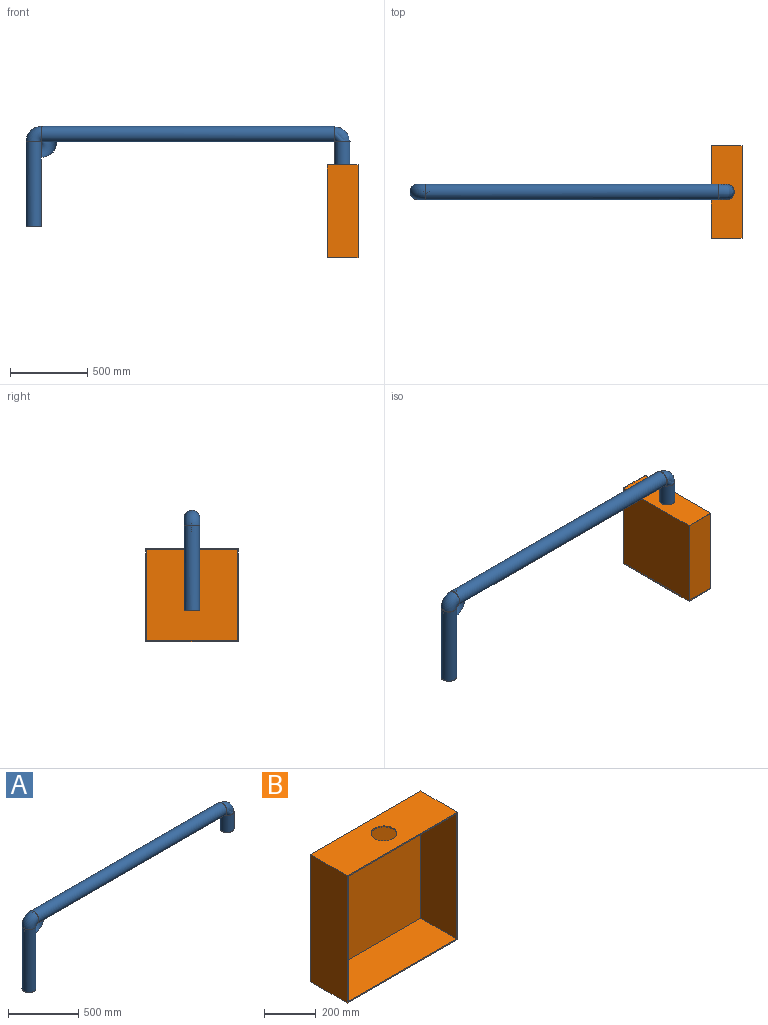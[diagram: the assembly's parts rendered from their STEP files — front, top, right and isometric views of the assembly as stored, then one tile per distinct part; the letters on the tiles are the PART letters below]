
ASSEMBLY  parts=2 mates=1
PART A: 12 faces, bbox 2116.5x100x658.2 mm
  f0: plane 100x100mm, normal (0,0,-1), area 914.2mm2, adj f2,f7
  f1: plane 100x100mm, normal (0,0,-1), area 914.2mm2, adj f6,f11
  f2: cylinder r=50mm len=550mm, axis (0,0,1), area 172787.6mm2, adj f0,f3
  f3: torus R=50mm, axis (0,1,0), area 24674mm2, adj f2,f4
  f4: cylinder r=50mm len=1900mm, axis (1,0,0), area 596902.6mm2, adj f3,f5
  f5: torus R=50mm, axis (0,1,0), area 24674mm2, adj f4,f6
  f6: cylinder r=50mm len=150mm, axis (0,0,-1), area 47123.9mm2, adj f1,f5
  f7: cylinder r=47mm len=550mm, axis (0,0,1), area 162420.3mm2, adj f0,f8
  f8: torus R=50mm, axis (0,1,0), area 23193.6mm2, adj f7,f9
  f9: cylinder r=47mm len=1900mm, axis (1,0,0), area 561088.4mm2, adj f8,f10
  f10: torus R=50mm, axis (0,1,0), area 23193.6mm2, adj f9,f11
  f11: cylinder r=47mm len=150mm, axis (0,0,-1), area 44296.5mm2, adj f1,f10
PART B: 12 faces, bbox 600x200x600 mm
  f0: plane 600x600mm, normal (0,-1,0), area 11900mm2, adj f1,f2,f3,f4,f6,f7,f8,f9
  f1: plane 600x200mm, normal (0,0,1), area 112146mm2, adj f0,f2,f4,f5,f11
  f2: plane 600x200mm, normal (-1,0,0), area 120000mm2, adj f0,f1,f3,f5
  f3: plane 600x200mm, normal (0,0,-1), area 120000mm2, adj f0,f2,f4,f5
  f4: plane 600x200mm, normal (1,0,0), area 120000mm2, adj f0,f1,f3,f5
  f5: plane 600x600mm, normal (0,1,0), area 360000mm2, adj f1,f2,f3,f4
  f6: plane 590x195mm, normal (0,0,-1), area 107196mm2, adj f0,f7,f9,f10,f11
  f7: plane 590x195mm, normal (1,0,0), area 115050mm2, adj f0,f6,f8,f10
  f8: plane 590x195mm, normal (0,0,1), area 115050mm2, adj f0,f7,f9,f10
  f9: plane 590x195mm, normal (-1,0,0), area 115050mm2, adj f0,f6,f8,f10
  f10: plane 590x590mm, normal (0,-1,0), area 348100mm2, adj f6,f7,f8,f9
  f11: cylinder r=50mm len=100mm, axis (0,0,1), area 1570.8mm2, adj f1,f6
PLACE A t=(-2759.94,-281.54,574.52)mm
PLACE B rot(axis=(0,0,1),90deg) t=(-859.94,-281.54,674.52)mm
MATE fastened B.f11 <-> A.f6  axis (0,0,1) through (-759.94,-281.54,974.52)mm
